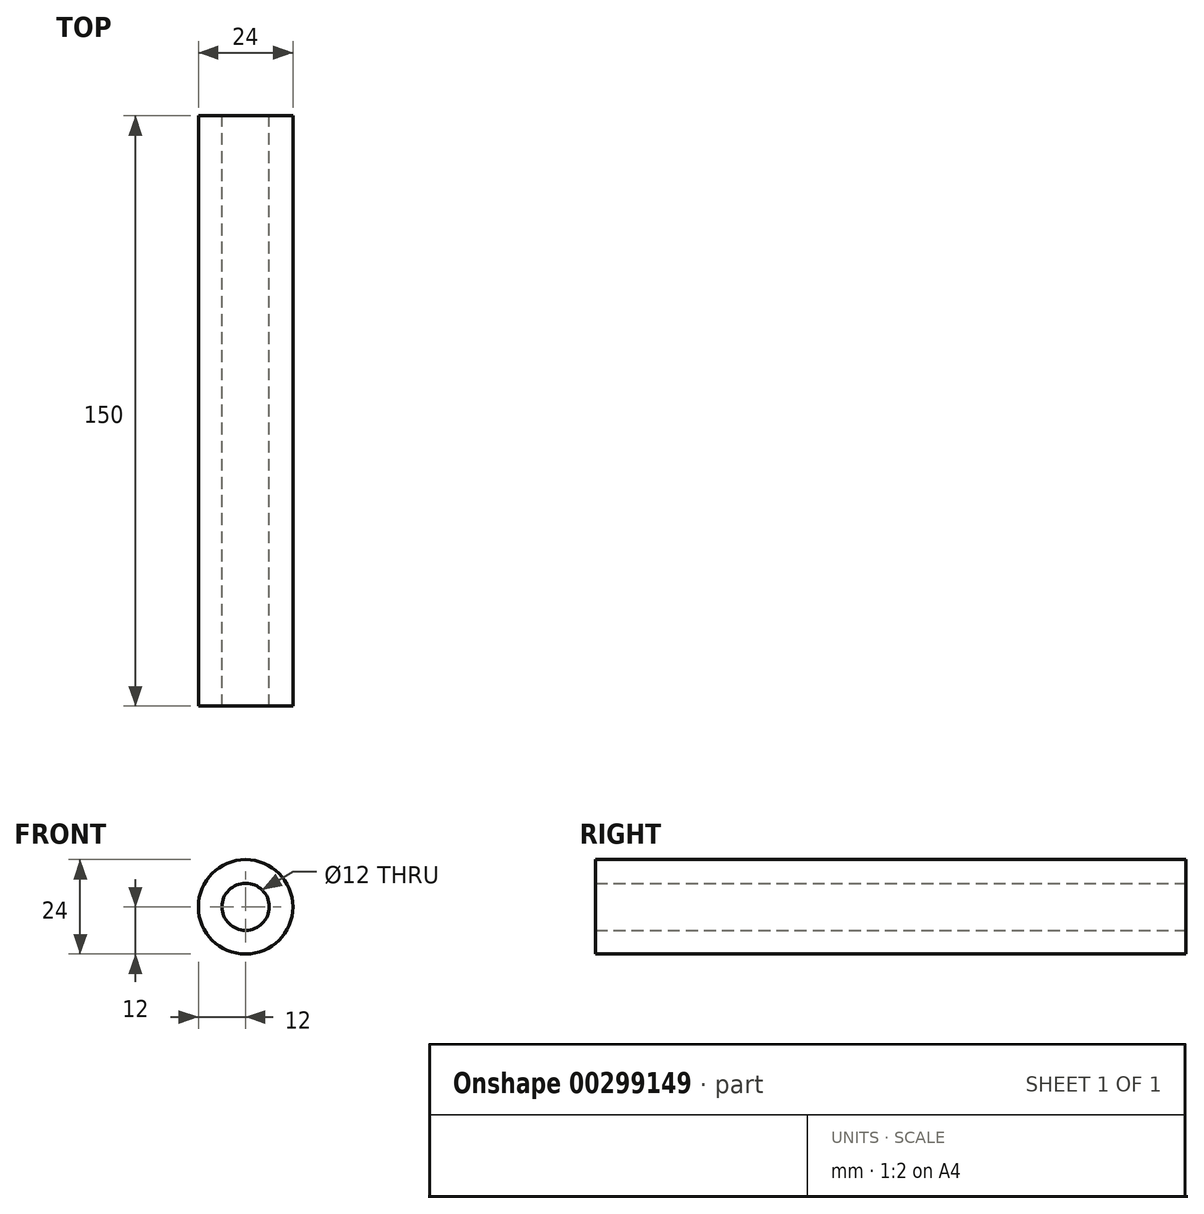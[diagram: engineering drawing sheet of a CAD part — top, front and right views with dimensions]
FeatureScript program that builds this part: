
annotation { "Feature Type Name" : "Feature", "Feature Type Description" : "" }
export const myFeature = defineFeature(function(context is Context, id is Id, definition is map)
    precondition{}
    {
        {
            var Q0;
            Q0=qCreatedBy(makeId("Front.planeOp"),FACE);
            var sketch = newSketch(context, id + "F0", { "sketchPlane" : qUnion([Q0])});
            skCircle(sketch, "E0", {"center": v(0, 0) * mm, "radius": 6 * mm});
            skCircle(sketch, "E1", {"center": v(0, 0) * mm, "radius": 12 * mm});
            skSolve(sketch);
        }
        {
            var Q0;
            Q0 = qSketchRegion(id + "F0", true);
            extrude(context, id + "F1", {"entities" : qUnion([Q0]), "depth" : 150 * mm});
        }
    });
